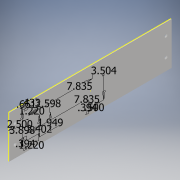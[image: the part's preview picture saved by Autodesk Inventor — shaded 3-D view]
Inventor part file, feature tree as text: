
AUTODESK INVENTOR PART (.ipt)
format: ipt  version: 2017 (Build 210142000, 142)  size: 152,064 bytes
history: native  units: in
note: dims shown in document units (in); Inventor stores cm internally (conversion verified against a paired STEP export)
features: other x2, hole x2, sketch x2, extrude x1
ambient origin geometry x8: Origin, YZ Plane, XZ Plane, XY Plane, X Axis, Y Axis, Z Axis, Center Point
bodies: Solid1 (feature_tree)
feature tree (7):
  extrude  "pdu nmt right side panel"  Depth=5.22in
  other  "snap psu"
  hole  "snap psu holes"  [1 undecoded]
  hole  "Hole4"  [1 undecoded]
  sketch  "Sketch1"  dims[d0=20.0in d1=5.22in]
  sketch  "Sketch5"  dims[d2=0.125in d3=0.0in d19=0.394in d20=1.22in d21=3.898in d22=0.5in d23=0.433in d24=0.661in d25=2.5in d26=0.134in d27=0.75in d28=0.248in d29=0.25in d30=90.0deg d31=1.0in d32=0.8108in d33=0.394in d34=3.504in d35=1.22in d36=2.402in d37=2.598in d38=1.949in d39=7.835in d40=7.835in d41=0.46in d42=4.3in d43=0.75in d44=0.46in d45=0.75in d46=4.3in d47=1.0in d48=0.236in d49=1.0in d50=0.236in d51=1.0in d53=1.0in d54=0.236in d55=0.236in d63=0.169in d64=0.75in d65=0.37in d66=0.25in d67=90.0deg d68=1.0in d69=0.8108in d70=0.18in d71=0.18in]
  other  "brackets"
note: 2 required parameter values undecoded (feature->parameter linkage not recoverable at this tier; creation-order binding heuristic only, values carry confidence <= 0.55)
